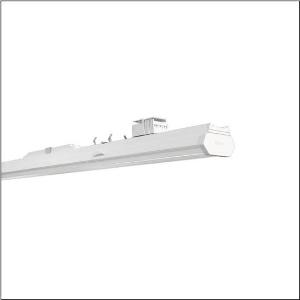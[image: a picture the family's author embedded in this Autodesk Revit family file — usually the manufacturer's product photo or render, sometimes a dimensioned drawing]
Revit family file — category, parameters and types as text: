
# Revit family: licross_21_protected_mo_52tp11cn49xg
name_source: partatom
category: Lighting Fixtures
units: mm (PartAtom-declared; Revit-internal decimal feet)

## family parameters
Cut with Voids When Loaded = No
Host = Face
Light Source = No
Part Type = Normal
Room Calculation Point = No
Round Connector Dimension = Use Diameter
Shared = No

## types (1)
- --- (1 x LED, 9070 lm, 50.4 W, 4000K)
    Apparent Load = 50 VA
    CIE Flux Codes = 83 94 98 100 100
    Color Rendering = 80
    Color Temperature = 4000K
    Default Elevation = 1800 mm
    Description = Licross 21 Protected MO, luminaire insert, of sheet steel, galvanised, coil coated, white, length: 1.500mm, width: 90mm, height: 103mm, LED rated luminous flux: 9.080lm, light colour: 840, SDCM (Standard Deviation of Colour Matching)MacAdam ≤ 3 SDCM (initial), control gear: ON/OFF Multilumen, CLOi, with plug, 3-pole, with phase selection, mains connection: 220..240V, AC, 50/60Hz, start of lifetime: 50W, end of service life: 61W, internal wiring halogen-free, primary light control with lens, of plastic, primary optical cover: cover, of PMMA, light emission: direct distribution, primary light characteristic: symmetric, protection rating (complete): IP64, insulation class (complete): insulation class I (protective earthing), certification: CE, ENEC, VDE, UKCA, protection symbol: D if used in an environment with conductive dust loads with corresponding accessories, impact resistance: IK06, permissible ambient temperature for indoor applications: -35..+45°C, corresponds to IFS (International Featured Standards) requirements for safety and quality in the food industry, reducing of maximum allowable ambient temperature of 5°C with ceiling mounting, LABS conformity tested according to VDMA 24364:2018-05, The light source and the operating device comply with the requirements of the Ecodesign Regulation (EU) 2019/2020 and are replaceable in accordance with this regulation, packaging unit: 1 piece
    Height = 92 mm
    Lamp = 1 x LED
    Lamp Light Flux = 9070 lm
    Lamp Power = 50.4 W
    Lamp count = 1
    Length = 1500 mm
    Luminous efficacy = 180 lm/W
    Manufacturer = Siteco
    ModVariant = No
    Model = 52TP11CN49XG
    Mounting Place = Ceiling
    Mounting Type = Pendant
    Number of Poles = 1
    OnlyDefault = Yes
    Power Factor = 1
    Product Name = Licross 21 Protected MO
    Product group = luminaire insert | ceiling pendant
    ProductGroupID = 901
    Protection Class = Protection class I
    Protection Degree = IP 64
    RLX_Detail_Level = 1
    RLX_Emergency_Light_Flux = 0 lm
    RLX_Emergency_Type = 0
    RLX_Emergency_Type_DB = No
    RlxData = <blob elided: 22245 chars, md5=923a2eca>
    Socket = socket
    Standby Power = 0 W
    System Light Flux = 9070 lm
    System Power = 50 W
    Type Comments = factory setting: luminous flux: 100 % | (A | C | E) | 117 mA
    Type Image = l_1256148.jpg
    URL = http://relux.com
    VarID = @adj_112365
    Voltage = 0 V
    Weight = 0.00 kg
    Width = 88 mm

## geometry (parser evidence)
native form markers: Blend x4, Sweep x9
no freeform markers — native parametric forms only
